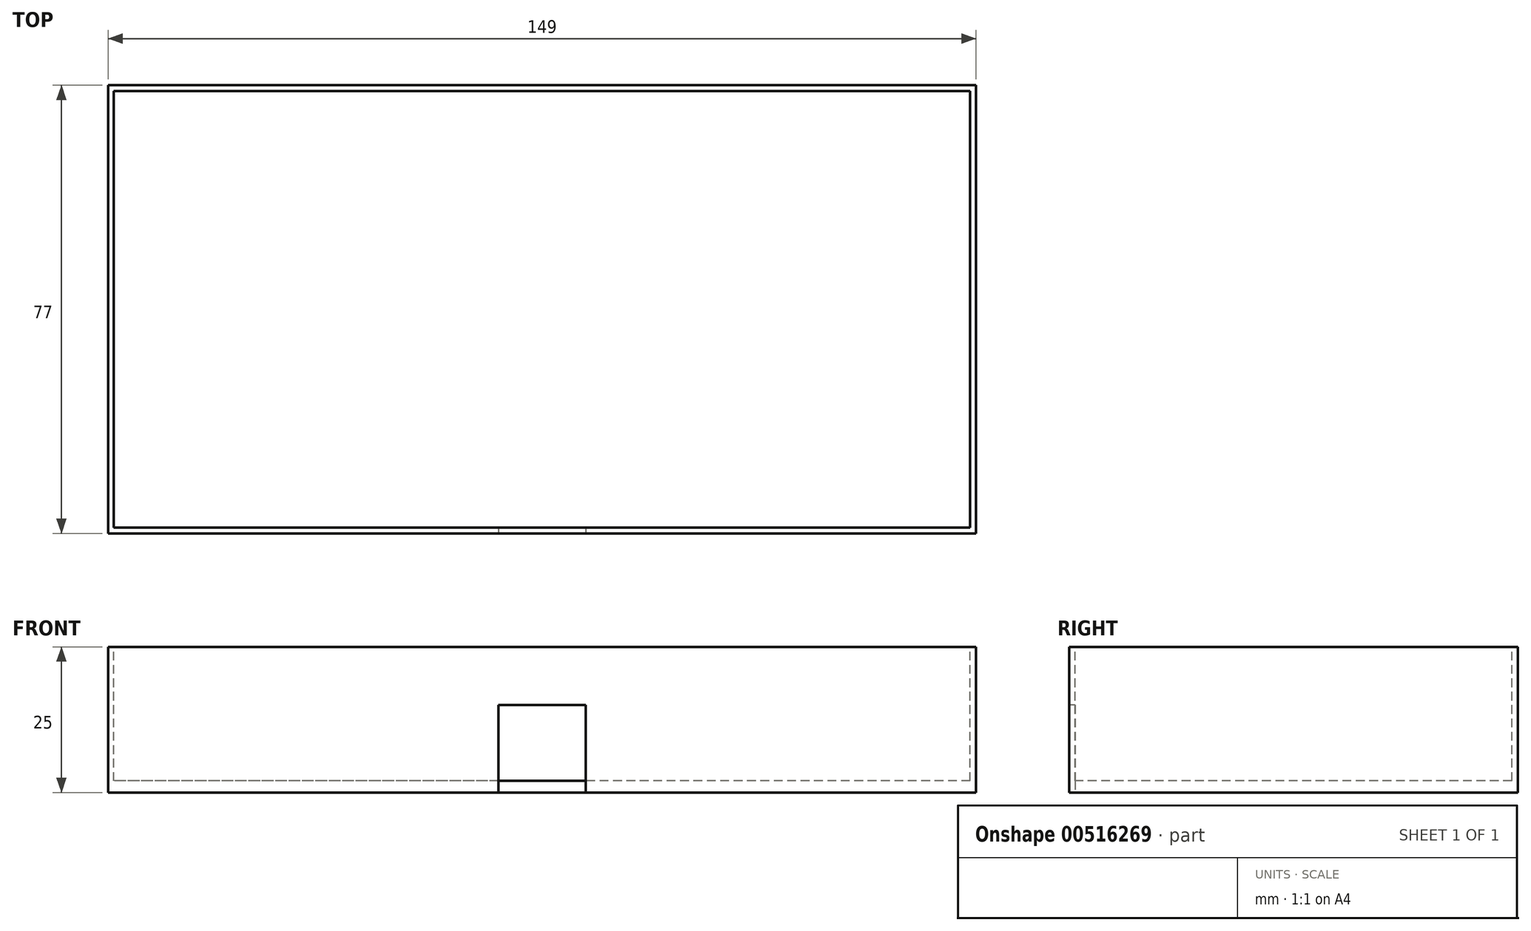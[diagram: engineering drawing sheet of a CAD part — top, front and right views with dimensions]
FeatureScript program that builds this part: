
annotation { "Feature Type Name" : "Feature", "Feature Type Description" : "" }
export const myFeature = defineFeature(function(context is Context, id is Id, definition is map)
    precondition{}
    {
        {
            var Q0;
            Q0=qCreatedBy(makeId("Top.planeOp"),FACE);
            var sketch = newSketch(context, id + "F0", { "sketchPlane" : qUnion([Q0])});
            skLineSegment(sketch, "E0.bottom", {"start": v(74.5, 38.5) * mm, "end": v(-74.5, 38.5) * mm});
            skLineSegment(sketch, "E0.top", {"start": v(74.5, -38.5) * mm, "end": v(-74.5, -38.5) * mm});
            skLineSegment(sketch, "E0.left", {"start": v(74.5, 38.5) * mm, "end": v(74.5, -38.5) * mm});
            skLineSegment(sketch, "E0.right", {"start": v(-74.5, 38.5) * mm, "end": v(-74.5, -38.5) * mm});
            skPoint(sketch, "E0.middle", {"position": v(0, 0) * mm});
            skSolve(sketch);
        }
        {
            var Q0;
            Q0=makeQuery(id+"F0.imprint","IMPRINT",FACE,{"disambiguationData":[TD([[makeQuery(id+"F0.imprint","IMPRINT",EDGE,{"derivedFrom":sQuery(id+"F0.wireOp",EDGE,"E0.bottom")}),1.0]])]});
            extrude(context, id + "F1", {"entities" : qUnion([Q0]), "depth" : 25 * mm});
        }
        {
            var Q0;
            Q0=makeQuery(id+"F1.opExtrude","CAP_FACE",FACE,{"disambiguationData":[OSD([sQuery(id+"F0.wireOp",EDGE,"E0.bottom"),sQuery(id+"F0.wireOp",EDGE,"E0.top"),sQuery(id+"F0.wireOp",EDGE,"E0.left"),sQuery(id+"F0.wireOp",EDGE,"E0.right")])],"isStart":false});
            var sketch = newSketch(context, id + "F2", { "sketchPlane" : qUnion([Q0])});
            skLineSegment(sketch, "E1.bottom", {"start": v(73.5, 37.5) * mm, "end": v(-73.5, 37.5) * mm});
            skLineSegment(sketch, "E1.top", {"start": v(73.5, -37.5) * mm, "end": v(-73.5, -37.5) * mm});
            skLineSegment(sketch, "E1.left", {"start": v(73.5, 37.5) * mm, "end": v(73.5, -37.5) * mm});
            skLineSegment(sketch, "E1.right", {"start": v(-73.5, 37.5) * mm, "end": v(-73.5, -37.5) * mm});
            skPoint(sketch, "E1.middle", {"position": v(0, 0) * mm});
            skSolve(sketch);
        }
        {
            var Q0;
            Q0=makeQuery(id+"F2.imprint","IMPRINT",FACE,{"disambiguationData":[TD([[makeQuery(id+"F2.imprint","IMPRINT",EDGE,{"derivedFrom":sQuery(id+"F2.wireOp",EDGE,"E1.bottom")}),1.0]])]});
            extrude(context, id + "F3", {"entities" : qUnion([Q0]), "operationType" : NewBodyOperationType.REMOVE, "oppositeDirection" : true, "depth" : 23 * mm});
        }
        {
            var Q0;
            Q0=makeQuery(id+"F1.opExtrude","SWEPT_FACE",FACE,{"disambiguationData":[OSD([sQuery(id+"F0.wireOp",EDGE,"E0.top")])]});
            var sketch = newSketch(context, id + "F4", { "sketchPlane" : qUnion([Q0])});
            skLineSegment(sketch, "E2.bottom", {"start": v(7.5, 15) * mm, "end": v(-7.5, 15) * mm});
            skLineSegment(sketch, "E2.top", {"start": v(7.5, -15) * mm, "end": v(-7.5, -15) * mm});
            skLineSegment(sketch, "E2.left", {"start": v(7.5, 15) * mm, "end": v(7.5, -15) * mm});
            skLineSegment(sketch, "E2.right", {"start": v(-7.5, 15) * mm, "end": v(-7.5, -15) * mm});
            skPoint(sketch, "E2.middle", {"position": v(0, 0) * mm});
            skSolve(sketch);
        }
        {
            var Q0;
            {var subQ0=sQuery(id+"F4.wireOp",EDGE,"E2.bottom");Q0=makeQuery(id+"F4.imprint","IMPRINT",FACE,{"disambiguationData":[TD([[makeQuery(id+"F4.imprint","IMPRINT",EDGE,{"derivedFrom":subQ0}),1.0]])]});}
            extrude(context, id + "F5", {"entities" : qUnion([Q0]), "operationType" : NewBodyOperationType.REMOVE, "oppositeDirection" : true, "depth" : 1 * mm});
        }
    });
